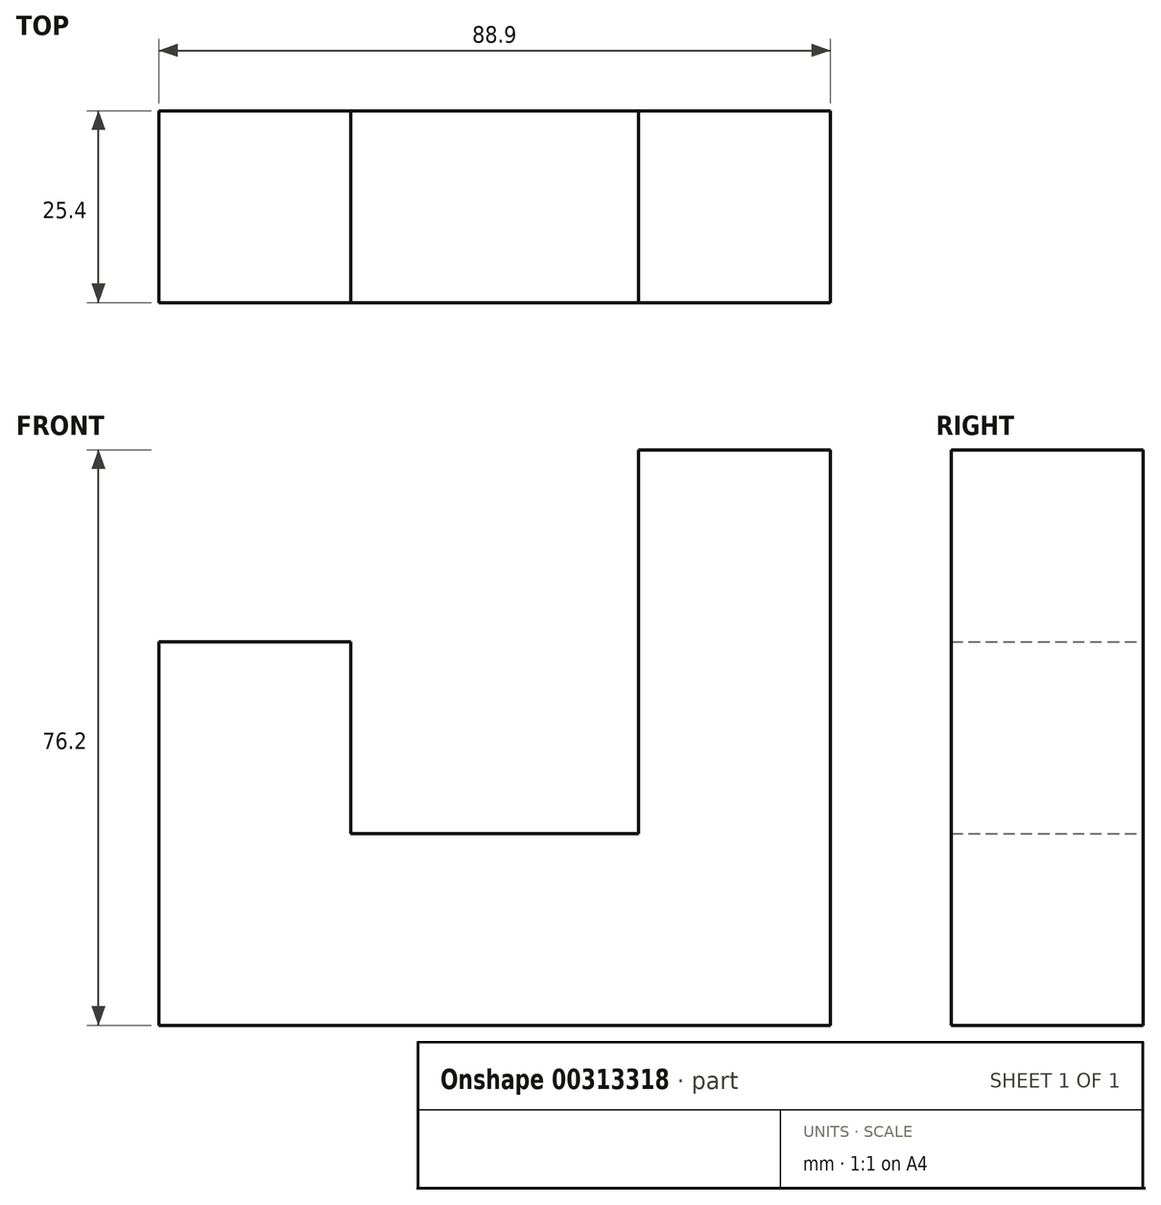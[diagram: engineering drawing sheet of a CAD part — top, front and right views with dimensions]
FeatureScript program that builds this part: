
annotation { "Feature Type Name" : "Feature", "Feature Type Description" : "" }
export const myFeature = defineFeature(function(context is Context, id is Id, definition is map)
    precondition{}
    {
        {
            var Q0;
            Q0=qCreatedBy(makeId("Front.planeOp"),FACE);
            var sketch = newSketch(context, id + "F0", { "sketchPlane" : qUnion([Q0])});
            skLineSegment(sketch, "E0", {"start": v(-44.45, -21.51) * mm, "end": v(44.45, -21.51) * mm});
            skLineSegment(sketch, "E1", {"start": v(-44.45, -21.51) * mm, "end": v(-44.45, 29.29) * mm});
            skLineSegment(sketch, "E2", {"start": v(44.45, -21.51) * mm, "end": v(44.45, 54.69) * mm});
            skLineSegment(sketch, "E3", {"start": v(-44.45, 29.29) * mm, "end": v(-19.05, 29.29) * mm});
            skLineSegment(sketch, "E4", {"start": v(44.45, 54.69) * mm, "end": v(19.05, 54.69) * mm});
            skLineSegment(sketch, "E5", {"start": v(-19.05, 29.29) * mm, "end": v(-19.05, 3.89) * mm});
            skLineSegment(sketch, "E6", {"start": v(19.05, 54.69) * mm, "end": v(19.05, 3.89) * mm});
            skLineSegment(sketch, "E7", {"start": v(-19.05, 3.89) * mm, "end": v(19.05, 3.89) * mm});
            skSolve(sketch);
        }
        {
            var Q0;
            Q0 = qSketchRegion(id + "F0", true);
            var Q1;
            Q1=makeQuery(id+"F0.imprint","IMPRINT",FACE,{"disambiguationData":[TD([[makeQuery(id+"F0.imprint","IMPRINT",EDGE,{"derivedFrom":sQuery(id+"F0.wireOp",EDGE,"E0")}),1.0]])]});
            extrude(context, id + "F1", {"entities" : qUnion([Q0, Q1]), "depth" : 25.4 * mm});
        }
    });
